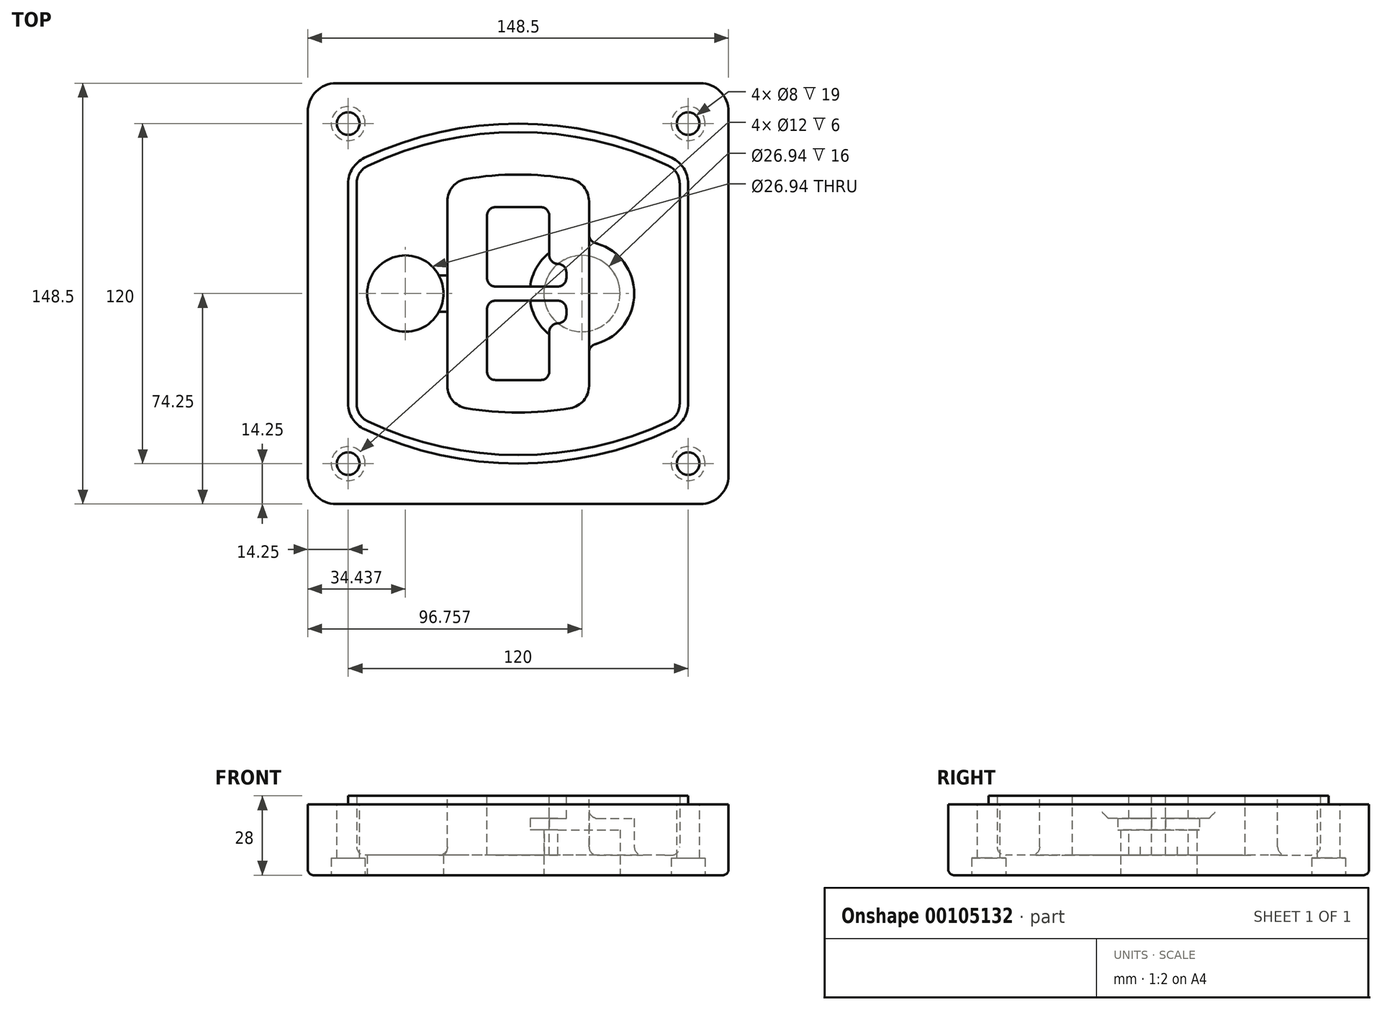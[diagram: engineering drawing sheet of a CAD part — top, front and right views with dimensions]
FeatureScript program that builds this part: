
annotation { "Feature Type Name" : "Feature", "Feature Type Description" : "" }
export const myFeature = defineFeature(function(context is Context, id is Id, definition is map)
    precondition{}
    {
        {
            var Q0;
            Q0=qCreatedBy(makeId("Top.planeOp"),FACE);
            var sketch = newSketch(context, id + "F0", { "sketchPlane" : qUnion([Q0])});
            skPoint(sketch, "E0.rect.middle", {"position": v(0, 0) * mm});
            skLineSegment(sketch, "E1.bottom", {"start": v(-64.25, -74.25) * mm, "end": v(64.25, -74.25) * mm});
            skLineSegment(sketch, "E1.top", {"start": v(-64.25, 74.25) * mm, "end": v(64.25, 74.25) * mm});
            skLineSegment(sketch, "E1.left", {"start": v(-74.25, -64.25) * mm, "end": v(-74.25, 64.25) * mm});
            skLineSegment(sketch, "E1.right", {"start": v(74.25, -64.25) * mm, "end": v(74.25, 64.25) * mm});
            skLineSegment(sketch, "E2", {"start": v(-74.25, 74.25) * mm, "end": v(74.25, -74.25) * mm, "construction": true});
            skLineSegment(sketch, "E3", {"start": v(74.25, 74.25) * mm, "end": v(-74.25, -74.25) * mm, "construction": true});
            skCircle(sketch, "E4", {"center": v(-60, 60) * mm, "radius": 4 * mm});
            skCircle(sketch, "E5", {"center": v(60, 60) * mm, "radius": 4 * mm});
            skCircle(sketch, "E6", {"center": v(60, -60) * mm, "radius": 4 * mm});
            skCircle(sketch, "E7", {"center": v(-60, -60) * mm, "radius": 4 * mm});
            skLineSegment(sketch, "E8", {"start": v(-60, 60) * mm, "end": v(60, 60) * mm, "construction": true});
            skLineSegment(sketch, "E9", {"start": v(60, 60) * mm, "end": v(60, -60) * mm, "construction": true});
            skLineSegment(sketch, "E10", {"start": v(60, -60) * mm, "end": v(-60, -60) * mm, "construction": true});
            skLineSegment(sketch, "E11", {"start": v(-60, -60) * mm, "end": v(-60, 60) * mm, "construction": true});
            skLineSegment(sketch, "E12", {"start": v(-60, 38.83) * mm, "end": v(-60, -38.83) * mm});
            skLineSegment(sketch, "E13", {"start": v(60, 38.83) * mm, "end": v(60, -38.83) * mm});
            skArc(sketch, "E14", {"start": v(54.26, 47.88) * mm, "mid": v(0, 60) * mm, "end": v(-54.26, 47.88) * mm});
            skArc(sketch, "E15", {"start": v(-54.26, -47.88) * mm, "mid": v(0, -60) * mm, "end": v(54.26, -47.88) * mm});
            skLineSegment(sketch, "E16", {"start": v(-60, 0) * mm, "end": v(60, 0) * mm, "construction": true});
            skPoint(sketch, "E17.visualSharp", {"position": v(-60, -45) * mm});
            skArc(sketch, "E17.filletArc", {"start": v(-60, -38.83) * mm, "mid": v(-58.44, -44.2) * mm, "end": v(-54.26, -47.88) * mm});
            skPoint(sketch, "E18.visualSharp", {"position": v(-60, 45) * mm});
            skArc(sketch, "E18.filletArc", {"start": v(-54.26, 47.88) * mm, "mid": v(-58.44, 44.2) * mm, "end": v(-60, 38.83) * mm});
            skPoint(sketch, "E19.visualSharp", {"position": v(60, 45) * mm});
            skArc(sketch, "E19.filletArc", {"start": v(60, 38.83) * mm, "mid": v(58.44, 44.2) * mm, "end": v(54.26, 47.88) * mm});
            skPoint(sketch, "E20.visualSharp", {"position": v(60, -45) * mm});
            skArc(sketch, "E20.filletArc", {"start": v(54.26, -47.88) * mm, "mid": v(58.44, -44.2) * mm, "end": v(60, -38.83) * mm});
            skPoint(sketch, "E21.visualSharp", {"position": v(-74.25, 74.25) * mm});
            skArc(sketch, "E21.filletArc", {"start": v(-64.25, 74.25) * mm, "mid": v(-71.32, 71.32) * mm, "end": v(-74.25, 64.25) * mm});
            skPoint(sketch, "E22.visualSharp", {"position": v(74.25, 74.25) * mm});
            skArc(sketch, "E22.filletArc", {"start": v(74.25, 64.25) * mm, "mid": v(71.32, 71.32) * mm, "end": v(64.25, 74.25) * mm});
            skPoint(sketch, "E23.visualSharp", {"position": v(74.25, -74.25) * mm});
            skArc(sketch, "E23.filletArc", {"start": v(64.25, -74.25) * mm, "mid": v(71.32, -71.32) * mm, "end": v(74.25, -64.25) * mm});
            skPoint(sketch, "E24.visualSharp", {"position": v(-74.25, -74.25) * mm});
            skArc(sketch, "E24.filletArc", {"start": v(-74.25, -64.25) * mm, "mid": v(-71.32, -71.32) * mm, "end": v(-64.25, -74.25) * mm});
            skArc(sketch, "E25.0", {"start": v(57, 38.83) * mm, "mid": v(55.9, 42.58) * mm, "end": v(52.98, 45.17) * mm});
            skLineSegment(sketch, "E25.1", {"start": v(57, 38.83) * mm, "end": v(57, -38.83) * mm});
            skArc(sketch, "E25.2", {"start": v(52.98, -45.17) * mm, "mid": v(55.9, -42.58) * mm, "end": v(57, -38.83) * mm});
            skArc(sketch, "E25.3", {"start": v(-52.98, -45.17) * mm, "mid": v(0, -57) * mm, "end": v(52.98, -45.17) * mm});
            skArc(sketch, "E25.4", {"start": v(-57, -38.83) * mm, "mid": v(-55.9, -42.58) * mm, "end": v(-52.98, -45.17) * mm});
            skArc(sketch, "E25.5", {"start": v(52.98, 45.17) * mm, "mid": v(0, 57) * mm, "end": v(-52.98, 45.17) * mm});
            skLineSegment(sketch, "E25.6", {"start": v(-57, 38.83) * mm, "end": v(-57, -38.83) * mm});
            skArc(sketch, "E25.7", {"start": v(-52.98, 45.17) * mm, "mid": v(-55.9, 42.58) * mm, "end": v(-57, 38.83) * mm});
            skArc(sketch, "E26.0", {"start": v(-55.96, 51.5) * mm, "mid": v(-61.82, 46.33) * mm, "end": v(-64, 38.83) * mm});
            skArc(sketch, "E26.1", {"start": v(55.96, 51.5) * mm, "mid": v(0, 64) * mm, "end": v(-55.96, 51.5) * mm});
            skArc(sketch, "E26.2", {"start": v(64, 38.83) * mm, "mid": v(61.82, 46.33) * mm, "end": v(55.96, 51.5) * mm});
            skLineSegment(sketch, "E26.3", {"start": v(64, 38.83) * mm, "end": v(64, -38.83) * mm});
            skArc(sketch, "E26.4", {"start": v(55.96, -51.5) * mm, "mid": v(61.82, -46.33) * mm, "end": v(64, -38.83) * mm});
            skLineSegment(sketch, "E26.5", {"start": v(-64, 38.83) * mm, "end": v(-64, -38.83) * mm});
            skArc(sketch, "E26.6", {"start": v(-55.96, -51.5) * mm, "mid": v(0, -64) * mm, "end": v(55.96, -51.5) * mm});
            skArc(sketch, "E26.7", {"start": v(-64, -38.83) * mm, "mid": v(-61.82, -46.33) * mm, "end": v(-55.96, -51.5) * mm});
            skSolve(sketch);
        }
        {
            var Q0;
            Q0=makeQuery(id+"F0.imprint","IMPRINT",FACE,{"disambiguationData":[TD([[makeQuery(id+"F0.imprint","IMPRINT",EDGE,{"derivedFrom":sQuery(id+"F0.wireOp",EDGE,"E1.bottom")}),1.0]])]});
            var Q1;
            Q1=makeQuery(id+"F0.imprint","IMPRINT",FACE,{"disambiguationData":[TD([[makeQuery(id+"F0.imprint","IMPRINT",EDGE,{"derivedFrom":sQuery(id+"F0.wireOp",EDGE,"E12")}),1.0]])]});
            var Q2;
            Q2=makeQuery(id+"F0.imprint","IMPRINT",FACE,{"disambiguationData":[TD([[makeQuery(id+"F0.imprint","IMPRINT",EDGE,{"derivedFrom":sQuery(id+"F0.wireOp",EDGE,"E25.0")}),1.0]])]});
            var Q3;
            Q3=makeQuery(id+"F0.imprint","IMPRINT",FACE,{"disambiguationData":[TD([[makeQuery(id+"F0.imprint","IMPRINT",EDGE,{"derivedFrom":sQuery(id+"F0.wireOp",EDGE,"E12")}),-1.0]])]});
            extrude(context, id + "F1", {"entities" : qUnion([Q0, Q1, Q2, Q3]), "oppositeDirection" : true, "depth" : 25 * mm});
        }
        {
            var Q0;
            Q0=makeQuery(id+"F0.imprint","IMPRINT",FACE,{"disambiguationData":[TD([[makeQuery(id+"F0.imprint","IMPRINT",EDGE,{"derivedFrom":sQuery(id+"F0.wireOp",EDGE,"E12")}),1.0]])]});
            extrude(context, id + "F2", {"entities" : qUnion([Q0]), "operationType" : NewBodyOperationType.ADD, "depth" : 3 * mm});
        }
        {
            var Q0;
            Q0=makeQuery(id+"F0.imprint","IMPRINT",FACE,{"disambiguationData":[TD([[makeQuery(id+"F0.imprint","IMPRINT",EDGE,{"derivedFrom":sQuery(id+"F0.wireOp",EDGE,"E25.0")}),1.0]])]});
            extrude(context, id + "F3", {"entities" : qUnion([Q0]), "operationType" : NewBodyOperationType.REMOVE, "oppositeDirection" : true, "depth" : 18 * mm});
        }
        {
            var Q0;
            Q0=makeQuery(id+"F2.opExtrude","CAP_FACE",FACE,{"disambiguationData":[OSD([sQuery(id+"F0.wireOp",EDGE,"E12"),sQuery(id+"F0.wireOp",EDGE,"E13"),sQuery(id+"F0.wireOp",EDGE,"E14"),sQuery(id+"F0.wireOp",EDGE,"E15"),sQuery(id+"F0.wireOp",EDGE,"E17.filletArc"),sQuery(id+"F0.wireOp",EDGE,"E18.filletArc"),sQuery(id+"F0.wireOp",EDGE,"E19.filletArc"),sQuery(id+"F0.wireOp",EDGE,"E20.filletArc"),sQuery(id+"F0.wireOp",EDGE,"E25.0"),sQuery(id+"F0.wireOp",EDGE,"E25.1"),sQuery(id+"F0.wireOp",EDGE,"E25.2"),sQuery(id+"F0.wireOp",EDGE,"E25.3"),sQuery(id+"F0.wireOp",EDGE,"E25.4"),sQuery(id+"F0.wireOp",EDGE,"E25.5"),sQuery(id+"F0.wireOp",EDGE,"E25.6"),sQuery(id+"F0.wireOp",EDGE,"E25.7")])],"isStart":false});
            var sketch = newSketch(context, id + "F4", { "sketchPlane" : qUnion([Q0])});
            skArc(sketch, "E27.0", {"start": v(-18.34, -40.45) * mm, "mid": v(0, -42) * mm, "end": v(18.34, -40.45) * mm});
            skArc(sketch, "E28.0", {"start": v(18.34, 40.45) * mm, "mid": v(0, 42) * mm, "end": v(-18.34, 40.45) * mm});
            skLineSegment(sketch, "E29", {"start": v(-25, 32.57) * mm, "end": v(-25, -32.57) * mm});
            skLineSegment(sketch, "E30", {"start": v(25, 32.57) * mm, "end": v(25, -32.57) * mm});
            skLineSegment(sketch, "E31", {"start": v(-25, 39.1) * mm, "end": v(25, 39.1) * mm, "construction": true});
            skLineSegment(sketch, "E32", {"start": v(-25, -39.1) * mm, "end": v(25, -39.1) * mm, "construction": true});
            skPoint(sketch, "E33.visualSharp", {"position": v(-25, 39.1) * mm});
            skArc(sketch, "E33.filletArc", {"start": v(-18.34, 40.45) * mm, "mid": v(-23.11, 37.73) * mm, "end": v(-25, 32.57) * mm});
            skPoint(sketch, "E34.visualSharp", {"position": v(25, 39.1) * mm});
            skArc(sketch, "E34.filletArc", {"start": v(25, 32.57) * mm, "mid": v(23.11, 37.73) * mm, "end": v(18.34, 40.45) * mm});
            skPoint(sketch, "E35.visualSharp", {"position": v(25, -39.1) * mm});
            skArc(sketch, "E35.filletArc", {"start": v(18.34, -40.45) * mm, "mid": v(23.11, -37.73) * mm, "end": v(25, -32.57) * mm});
            skPoint(sketch, "E36.visualSharp", {"position": v(-25, -39.1) * mm});
            skArc(sketch, "E36.filletArc", {"start": v(-25, -32.57) * mm, "mid": v(-23.11, -37.73) * mm, "end": v(-18.34, -40.45) * mm});
            skArc(sketch, "E37.0", {"start": v(52.98, 45.17) * mm, "mid": v(0, 57) * mm, "end": v(-52.98, 45.17) * mm});
            skArc(sketch, "E37.1", {"start": v(-52.98, 45.17) * mm, "mid": v(-55.9, 42.58) * mm, "end": v(-57, 38.83) * mm});
            skLineSegment(sketch, "E37.2", {"start": v(-57, 38.83) * mm, "end": v(-57, -38.83) * mm});
            skArc(sketch, "E37.3", {"start": v(-57, -38.83) * mm, "mid": v(-55.9, -42.58) * mm, "end": v(-52.98, -45.17) * mm});
            skArc(sketch, "E37.4", {"start": v(-52.98, -45.17) * mm, "mid": v(0, -57) * mm, "end": v(52.98, -45.17) * mm});
            skArc(sketch, "E37.5", {"start": v(52.98, -45.17) * mm, "mid": v(55.9, -42.58) * mm, "end": v(57, -38.83) * mm});
            skLineSegment(sketch, "E37.6", {"start": v(57, 38.83) * mm, "end": v(57, -38.83) * mm});
            skArc(sketch, "E37.7", {"start": v(57, 38.83) * mm, "mid": v(55.9, 42.58) * mm, "end": v(52.98, 45.17) * mm});
            skLineSegment(sketch, "E38.0", {"start": v(23, 32.57) * mm, "end": v(23, -32.57) * mm});
            skArc(sketch, "E38.1", {"start": v(18, -38.48) * mm, "mid": v(21.58, -36.44) * mm, "end": v(23, -32.57) * mm});
            skArc(sketch, "E38.2", {"start": v(-18, -38.48) * mm, "mid": v(0, -40) * mm, "end": v(18, -38.48) * mm});
            skArc(sketch, "E38.3", {"start": v(-23, -32.57) * mm, "mid": v(-21.58, -36.44) * mm, "end": v(-18, -38.48) * mm});
            skLineSegment(sketch, "E38.4", {"start": v(-23, 32.57) * mm, "end": v(-23, -32.57) * mm});
            skArc(sketch, "E38.5", {"start": v(23, 32.57) * mm, "mid": v(21.58, 36.44) * mm, "end": v(18, 38.48) * mm});
            skArc(sketch, "E38.6", {"start": v(-18, 38.48) * mm, "mid": v(-21.58, 36.44) * mm, "end": v(-23, 32.57) * mm});
            skArc(sketch, "E38.7", {"start": v(18, 38.48) * mm, "mid": v(0, 40) * mm, "end": v(-18, 38.48) * mm});
            skArc(sketch, "E39.0", {"start": v(21, 32.57) * mm, "mid": v(20.06, 35.15) * mm, "end": v(17.67, 36.5) * mm});
            skLineSegment(sketch, "E39.1", {"start": v(21, 32.57) * mm, "end": v(21, -32.57) * mm});
            skArc(sketch, "E39.2", {"start": v(17.67, -36.5) * mm, "mid": v(20.06, -35.15) * mm, "end": v(21, -32.57) * mm});
            skArc(sketch, "E39.3", {"start": v(-17.67, -36.5) * mm, "mid": v(0, -38) * mm, "end": v(17.67, -36.5) * mm});
            skArc(sketch, "E39.4", {"start": v(-21, -32.57) * mm, "mid": v(-20.06, -35.15) * mm, "end": v(-17.67, -36.5) * mm});
            skArc(sketch, "E39.5", {"start": v(17.67, 36.5) * mm, "mid": v(0, 38) * mm, "end": v(-17.67, 36.5) * mm});
            skLineSegment(sketch, "E39.6", {"start": v(-21, 32.57) * mm, "end": v(-21, -32.57) * mm});
            skArc(sketch, "E39.7", {"start": v(-17.67, 36.5) * mm, "mid": v(-20.06, 35.15) * mm, "end": v(-21, 32.57) * mm});
            skLineSegment(sketch, "E40", {"start": v(-25, 0) * mm, "end": v(25, 0) * mm, "construction": true});
            skLineSegment(sketch, "E41", {"start": v(-11, 5.5) * mm, "end": v(-11, 27.5) * mm});
            skLineSegment(sketch, "E42", {"start": v(-8, 30.5) * mm, "end": v(8, 30.5) * mm});
            skLineSegment(sketch, "E43", {"start": v(11, 27.5) * mm, "end": v(11, 13.5) * mm});
            skLineSegment(sketch, "E44", {"start": v(14, 10.5) * mm, "end": v(14, 10.5) * mm});
            skLineSegment(sketch, "E45", {"start": v(17, 7.5) * mm, "end": v(17, 5.5) * mm});
            skLineSegment(sketch, "E46", {"start": v(14, 2.5) * mm, "end": v(-8, 2.5) * mm});
            skPoint(sketch, "E47.visualSharp", {"position": v(-11, 30.5) * mm});
            skArc(sketch, "E47.filletArc", {"start": v(-8, 30.5) * mm, "mid": v(-10.12, 29.62) * mm, "end": v(-11, 27.5) * mm});
            skPoint(sketch, "E48.visualSharp", {"position": v(11, 30.5) * mm});
            skArc(sketch, "E48.filletArc", {"start": v(11, 27.5) * mm, "mid": v(10.12, 29.62) * mm, "end": v(8, 30.5) * mm});
            skPoint(sketch, "E49.visualSharp", {"position": v(11, 10.5) * mm});
            skArc(sketch, "E49.filletArc", {"start": v(11, 13.5) * mm, "mid": v(11.88, 11.38) * mm, "end": v(14, 10.5) * mm});
            skPoint(sketch, "E50.visualSharp", {"position": v(17, 10.5) * mm});
            skArc(sketch, "E50.filletArc", {"start": v(17, 7.5) * mm, "mid": v(16.12, 9.62) * mm, "end": v(14, 10.5) * mm});
            skPoint(sketch, "E51.visualSharp", {"position": v(17, 2.5) * mm});
            skArc(sketch, "E51.filletArc", {"start": v(14, 2.5) * mm, "mid": v(16.12, 3.38) * mm, "end": v(17, 5.5) * mm});
            skPoint(sketch, "E52.visualSharp", {"position": v(-11, 2.5) * mm});
            skArc(sketch, "E52.filletArc", {"start": v(-11, 5.5) * mm, "mid": v(-10.12, 3.38) * mm, "end": v(-8, 2.5) * mm});
            skLineSegment(sketch, "E53.0.MirrorCS", {"start": v(14, -2.5) * mm, "end": v(-8, -2.5) * mm});
            skArc(sketch, "E54.0.MirrorCS", {"start": v(-11, -5.5) * mm, "mid": v(-10.12, -3.38) * mm, "end": v(-8, -2.5) * mm});
            skLineSegment(sketch, "E55.0.MirrorCS", {"start": v(-11, -5.5) * mm, "end": v(-11, -27.5) * mm});
            skArc(sketch, "E56.0.MirrorCS", {"start": v(-8, -30.5) * mm, "mid": v(-10.12, -29.62) * mm, "end": v(-11, -27.5) * mm});
            skLineSegment(sketch, "E57.0.MirrorCS", {"start": v(-8, -30.5) * mm, "end": v(8, -30.5) * mm});
            skArc(sketch, "E58.0.MirrorCS", {"start": v(11, -27.5) * mm, "mid": v(10.12, -29.62) * mm, "end": v(8, -30.5) * mm});
            skLineSegment(sketch, "E59.0.MirrorCS", {"start": v(11, -27.5) * mm, "end": v(11, -13.5) * mm});
            skArc(sketch, "E60.0.MirrorCS", {"start": v(11, -13.5) * mm, "mid": v(11.88, -11.38) * mm, "end": v(14, -10.5) * mm});
            skArc(sketch, "E61.0.MirrorCS", {"start": v(17, -7.5) * mm, "mid": v(16.12, -9.62) * mm, "end": v(14, -10.5) * mm});
            skLineSegment(sketch, "E62.0.MirrorCS", {"start": v(17, -7.5) * mm, "end": v(17, -5.5) * mm});
            skArc(sketch, "E63.0.MirrorCS", {"start": v(14, -2.5) * mm, "mid": v(16.12, -3.38) * mm, "end": v(17, -5.5) * mm});
            skSolve(sketch);
        }
        {
            var Q0;
            Q0=makeQuery(id+"F4.imprint","IMPRINT",FACE,{"disambiguationData":[TD([[makeQuery(id+"F4.imprint","IMPRINT",EDGE,{"derivedFrom":sQuery(id+"F4.wireOp",EDGE,"E27.0")}),1.0]])]});
            var Q1;
            Q1=makeQuery(id+"F4.imprint","IMPRINT",FACE,{"disambiguationData":[TD([[makeQuery(id+"F4.imprint","IMPRINT",EDGE,{"derivedFrom":sQuery(id+"F4.wireOp",EDGE,"E38.0")}),-1.0]])]});
            var Q2;
            Q2=makeQuery(id+"F4.imprint","IMPRINT",FACE,{"disambiguationData":[TD([[makeQuery(id+"F4.imprint","IMPRINT",EDGE,{"derivedFrom":sQuery(id+"F4.wireOp",EDGE,"E39.0")}),1.0]])]});
            extrude(context, id + "F5", {"entities" : qUnion([Q0, Q1, Q2]), "operationType" : NewBodyOperationType.ADD, "endBound" : BoundingType.UP_TO_NEXT, "oppositeDirection" : true, "depth" : 25 * mm});
        }
        {
            var Q0;
            Q0=makeQuery(id+"F1.opExtrude","CAP_FACE",FACE,{"disambiguationData":[OSD([sQuery(id+"F0.wireOp",EDGE,"E1.bottom"),sQuery(id+"F0.wireOp",EDGE,"E1.top"),sQuery(id+"F0.wireOp",EDGE,"E1.left"),sQuery(id+"F0.wireOp",EDGE,"E1.right"),sQuery(id+"F0.wireOp",EDGE,"E4"),sQuery(id+"F0.wireOp",EDGE,"E5"),sQuery(id+"F0.wireOp",EDGE,"E6"),sQuery(id+"F0.wireOp",EDGE,"E7"),sQuery(id+"F0.wireOp",EDGE,"E21.filletArc"),sQuery(id+"F0.wireOp",EDGE,"E22.filletArc"),sQuery(id+"F0.wireOp",EDGE,"E23.filletArc"),sQuery(id+"F0.wireOp",EDGE,"E24.filletArc")])],"isStart":false});
            var sketch = newSketch(context, id + "F6", { "sketchPlane" : qUnion([Q0])});
            skCircle(sketch, "E64", {"center": v(22.5, 0) * mm, "radius": 13.47 * mm});
            skCircle(sketch, "E65", {"center": v(-39.81, 0) * mm, "radius": 13.47 * mm});
            skLineSegment(sketch, "E66", {"start": v(74.25, 0) * mm, "end": v(-74.25, 0) * mm});
            skCircle(sketch, "E67", {"center": v(22.5, 0) * mm, "radius": 18.47 * mm});
            skCircle(sketch, "E68", {"center": v(60, -60) * mm, "radius": 6 * mm});
            skCircle(sketch, "E69", {"center": v(-60, -60) * mm, "radius": 6 * mm});
            skCircle(sketch, "E70", {"center": v(-60, 60) * mm, "radius": 6 * mm});
            skCircle(sketch, "E71", {"center": v(60, 60) * mm, "radius": 6 * mm});
            skSolve(sketch);
        }
        {
            var Q0;
            {var subQ1=sQuery(id+"F6.wireOp",EDGE,"E66");var subQ4=sQuery(id+"F6.wireOp",EDGE,"E64");var subQ6=makeQuery(id+"F6.imprint","INTERSECT",VERTEX,{"disambiguationData":[OD(0.0)],"derivedFrom":[subQ4,subQ1]});Q0=makeQuery(id+"F6.imprint","IMPRINT",FACE,{"disambiguationData":[TD([[makeQuery(id+"F6.imprint","IMPRINT",EDGE,{"disambiguationData":[TD([[subQ6,-1.0]])],"derivedFrom":subQ4}),-1.0]])]});}
            var Q1;
            {var subQ0=sQuery(id+"F6.wireOp",EDGE,"E66");var subQ1=sQuery(id+"F6.wireOp",EDGE,"E64");var subQ3=makeQuery(id+"F6.imprint","INTERSECT",VERTEX,{"disambiguationData":[OD(0.0)],"derivedFrom":[subQ1,subQ0]});Q1=makeQuery(id+"F6.imprint","IMPRINT",FACE,{"disambiguationData":[TD([[makeQuery(id+"F6.imprint","IMPRINT",EDGE,{"disambiguationData":[TD([[subQ3,-1.0]])],"derivedFrom":subQ1}),1.0]])]});}
            var Q2;
            {var subQ0=sQuery(id+"F6.wireOp",EDGE,"E66");var subQ1=sQuery(id+"F6.wireOp",EDGE,"E64");var subQ3=makeQuery(id+"F6.imprint","INTERSECT",VERTEX,{"disambiguationData":[OD(0.0)],"derivedFrom":[subQ1,subQ0]});Q2=makeQuery(id+"F6.imprint","IMPRINT",FACE,{"disambiguationData":[TD([[makeQuery(id+"F6.imprint","IMPRINT",EDGE,{"disambiguationData":[TD([[subQ3,1.0]])],"derivedFrom":subQ1}),1.0]])]});}
            var Q3;
            {var subQ1=sQuery(id+"F6.wireOp",EDGE,"E66");var subQ4=sQuery(id+"F6.wireOp",EDGE,"E64");var subQ6=makeQuery(id+"F6.imprint","INTERSECT",VERTEX,{"disambiguationData":[OD(0.0)],"derivedFrom":[subQ4,subQ1]});Q3=makeQuery(id+"F6.imprint","IMPRINT",FACE,{"disambiguationData":[TD([[makeQuery(id+"F6.imprint","IMPRINT",EDGE,{"disambiguationData":[TD([[subQ6,1.0]])],"derivedFrom":subQ4}),-1.0]])]});}
            extrude(context, id + "F7", {"entities" : qUnion([Q0, Q1, Q2, Q3]), "operationType" : NewBodyOperationType.ADD, "oppositeDirection" : true, "depth" : 20 * mm});
        }
        {
            var Q0;
            {var subQ0=sQuery(id+"F6.wireOp",EDGE,"E66");var subQ1=sQuery(id+"F6.wireOp",EDGE,"E64");var subQ3=makeQuery(id+"F6.imprint","INTERSECT",VERTEX,{"disambiguationData":[OD(0.0)],"derivedFrom":[subQ1,subQ0]});Q0=makeQuery(id+"F6.imprint","IMPRINT",FACE,{"disambiguationData":[TD([[makeQuery(id+"F6.imprint","IMPRINT",EDGE,{"disambiguationData":[TD([[subQ3,-1.0]])],"derivedFrom":subQ1}),1.0]])]});}
            var Q1;
            {var subQ0=sQuery(id+"F6.wireOp",EDGE,"E66");var subQ1=sQuery(id+"F6.wireOp",EDGE,"E64");var subQ3=makeQuery(id+"F6.imprint","INTERSECT",VERTEX,{"disambiguationData":[OD(0.0)],"derivedFrom":[subQ1,subQ0]});Q1=makeQuery(id+"F6.imprint","IMPRINT",FACE,{"disambiguationData":[TD([[makeQuery(id+"F6.imprint","IMPRINT",EDGE,{"disambiguationData":[TD([[subQ3,1.0]])],"derivedFrom":subQ1}),1.0]])]});}
            extrude(context, id + "F8", {"entities" : qUnion([Q0, Q1]), "operationType" : NewBodyOperationType.REMOVE, "oppositeDirection" : true, "depth" : 16 * mm});
        }
        {
            var Q0;
            {var subQ0=sQuery(id+"F6.wireOp",EDGE,"E66");var subQ1=sQuery(id+"F6.wireOp",EDGE,"E65");var subQ3=makeQuery(id+"F6.imprint","INTERSECT",VERTEX,{"disambiguationData":[OD(0.0)],"derivedFrom":[subQ1,subQ0]});Q0=makeQuery(id+"F6.imprint","IMPRINT",FACE,{"disambiguationData":[TD([[makeQuery(id+"F6.imprint","IMPRINT",EDGE,{"disambiguationData":[TD([[subQ3,-1.0]])],"derivedFrom":subQ1}),1.0]])]});}
            var Q1;
            {var subQ0=sQuery(id+"F6.wireOp",EDGE,"E66");var subQ1=sQuery(id+"F6.wireOp",EDGE,"E65");var subQ3=makeQuery(id+"F6.imprint","INTERSECT",VERTEX,{"disambiguationData":[OD(0.0)],"derivedFrom":[subQ1,subQ0]});Q1=makeQuery(id+"F6.imprint","IMPRINT",FACE,{"disambiguationData":[TD([[makeQuery(id+"F6.imprint","IMPRINT",EDGE,{"disambiguationData":[TD([[subQ3,1.0]])],"derivedFrom":subQ1}),1.0]])]});}
            extrude(context, id + "F9", {"entities" : qUnion([Q0, Q1]), "operationType" : NewBodyOperationType.REMOVE, "oppositeDirection" : true, "depth" : 25 * mm});
        }
        {
            var Q0;
            Q0=makeQuery(id+"F6.imprint","IMPRINT",FACE,{"disambiguationData":[TD([[makeQuery(id+"F6.imprint","IMPRINT",EDGE,{"derivedFrom":sQuery(id+"F6.wireOp",EDGE,"E68")}),1.0]])]});
            var Q1;
            Q1=makeQuery(id+"F6.imprint","IMPRINT",FACE,{"disambiguationData":[TD([[makeQuery(id+"F6.imprint","IMPRINT",EDGE,{"derivedFrom":makeQuery(id+"F1.opExtrude","CAP_EDGE",EDGE,{"disambiguationData":[OSD([sQuery(id+"F0.wireOp",EDGE,"E5")])],"isStart":false})}),-1.0]])]});
            var Q2;
            Q2=makeQuery(id+"F6.imprint","IMPRINT",FACE,{"disambiguationData":[TD([[makeQuery(id+"F6.imprint","IMPRINT",EDGE,{"derivedFrom":sQuery(id+"F6.wireOp",EDGE,"E69")}),1.0]])]});
            var Q3;
            Q3=makeQuery(id+"F6.imprint","IMPRINT",FACE,{"disambiguationData":[TD([[makeQuery(id+"F6.imprint","IMPRINT",EDGE,{"derivedFrom":makeQuery(id+"F1.opExtrude","CAP_EDGE",EDGE,{"disambiguationData":[OSD([sQuery(id+"F0.wireOp",EDGE,"E4")])],"isStart":false})}),-1.0]])]});
            var Q4;
            Q4=makeQuery(id+"F6.imprint","IMPRINT",FACE,{"disambiguationData":[TD([[makeQuery(id+"F6.imprint","IMPRINT",EDGE,{"derivedFrom":sQuery(id+"F6.wireOp",EDGE,"E70")}),1.0]])]});
            var Q5;
            Q5=makeQuery(id+"F6.imprint","IMPRINT",FACE,{"disambiguationData":[TD([[makeQuery(id+"F6.imprint","IMPRINT",EDGE,{"derivedFrom":makeQuery(id+"F1.opExtrude","CAP_EDGE",EDGE,{"disambiguationData":[OSD([sQuery(id+"F0.wireOp",EDGE,"E7")])],"isStart":false})}),-1.0]])]});
            var Q6;
            Q6=makeQuery(id+"F6.imprint","IMPRINT",FACE,{"disambiguationData":[TD([[makeQuery(id+"F6.imprint","IMPRINT",EDGE,{"derivedFrom":sQuery(id+"F6.wireOp",EDGE,"E71")}),1.0]])]});
            var Q7;
            Q7=makeQuery(id+"F6.imprint","IMPRINT",FACE,{"disambiguationData":[TD([[makeQuery(id+"F6.imprint","IMPRINT",EDGE,{"derivedFrom":makeQuery(id+"F1.opExtrude","CAP_EDGE",EDGE,{"disambiguationData":[OSD([sQuery(id+"F0.wireOp",EDGE,"E6")])],"isStart":false})}),-1.0]])]});
            extrude(context, id + "F10", {"entities" : qUnion([Q0, Q1, Q2, Q3, Q4, Q5, Q6, Q7]), "operationType" : NewBodyOperationType.REMOVE, "oppositeDirection" : true, "depth" : 6 * mm});
        }
        {
            var Q0;
            Q0=makeQuery(id+"F8.boolean.opBoolean","COPY",FACE,{"derivedFrom":makeQuery(id+"F8.opExtrude","CAP_FACE",FACE,{"disambiguationData":[OSD([sQuery(id+"F6.wireOp",EDGE,"E64")])],"isStart":false})});
            var sketch = newSketch(context, id + "F11", { "sketchPlane" : qUnion([Q0])});
            skArc(sketch, "E72.0", {"start": v(11, 14.45) * mm, "mid": v(6.45, 9.13) * mm, "end": v(4.2, 2.5) * mm});
            skArc(sketch, "E72.1", {"start": v(4.2, -2.5) * mm, "mid": v(6.45, -9.13) * mm, "end": v(11, -14.45) * mm});
            skLineSegment(sketch, "E73", {"start": v(4.2, -2.5) * mm, "end": v(14, -2.5) * mm});
            skLineSegment(sketch, "E74.0", {"start": v(14, 2.5) * mm, "end": v(4.2, 2.5) * mm});
            skArc(sketch, "E74.1", {"start": v(14, 2.5) * mm, "mid": v(16.12, 3.38) * mm, "end": v(17, 5.5) * mm});
            skLineSegment(sketch, "E74.2", {"start": v(17, 7.5) * mm, "end": v(17, 5.5) * mm});
            skArc(sketch, "E74.3", {"start": v(17, 7.5) * mm, "mid": v(16.12, 9.62) * mm, "end": v(14, 10.5) * mm});
            skArc(sketch, "E74.4", {"start": v(11, 13.5) * mm, "mid": v(11.88, 11.38) * mm, "end": v(14, 10.5) * mm});
            skLineSegment(sketch, "E74.5", {"start": v(11, 14.45) * mm, "end": v(11, 13.5) * mm});
            skLineSegment(sketch, "E74.7", {"start": v(14, -2.5) * mm, "end": v(4.2, -2.5) * mm});
            skArc(sketch, "E74.8", {"start": v(14, -2.5) * mm, "mid": v(16.12, -3.38) * mm, "end": v(17, -5.5) * mm});
            skLineSegment(sketch, "E74.9", {"start": v(17, -7.5) * mm, "end": v(17, -5.5) * mm});
            skArc(sketch, "E74.10", {"start": v(17, -7.5) * mm, "mid": v(16.12, -9.62) * mm, "end": v(14, -10.5) * mm});
            skArc(sketch, "E74.11", {"start": v(11, -13.5) * mm, "mid": v(11.88, -11.38) * mm, "end": v(14, -10.5) * mm});
            skLineSegment(sketch, "E74.12", {"start": v(11, -14.45) * mm, "end": v(11, -13.5) * mm});
            skPoint(sketch, "E75.orphan", {"position": v(11, -27.5) * mm});
            skPoint(sketch, "E76.orphan", {"position": v(-8, -2.5) * mm});
            skPoint(sketch, "E77.orphan", {"position": v(-8, 2.5) * mm});
            skPoint(sketch, "E78.orphan", {"position": v(11, 27.5) * mm});
            skSolve(sketch);
        }
        {
            var Q0;
            {var subQ7=sQuery(id+"F11.wireOp",EDGE,"E72.0");var subQ14=sQuery(id+"F11.wireOp",EDGE,"E72.1");var subQ16=sQuery(id+"F11.wireOp",EDGE,"E74.1");var subQ18=sQuery(id+"F11.wireOp",EDGE,"E74.8");Q0=qUnion([makeQuery(id+"F11.imprint","IMPRINT",FACE,{"disambiguationData":[TD([[makeQuery(id+"F11.imprint","IMPRINT",EDGE,{"derivedFrom":subQ7}),1.0]])]}),makeQuery(id+"F11.imprint","IMPRINT",FACE,{"disambiguationData":[TD([[makeQuery(id+"F11.imprint","IMPRINT",EDGE,{"derivedFrom":subQ14}),1.0]])]}),makeQuery(id+"F11.imprint","IMPRINT",FACE,{"disambiguationData":[TD([[makeQuery(id+"F11.imprint","IMPRINT",EDGE,{"derivedFrom":subQ16}),1.0]])]}),makeQuery(id+"F11.imprint","IMPRINT",FACE,{"disambiguationData":[TD([[makeQuery(id+"F11.imprint","IMPRINT",EDGE,{"derivedFrom":subQ18}),-1.0]])]})]);}
            var Q1;
            Q1=makeQuery(id+"F5.boolean.opBoolean","SPLIT",FACE,{"disambiguationData":[TD([makeQuery(id+"F5.opExtrude","SWEPT_FACE",FACE,{"disambiguationData":[OSD([sQuery(id+"F4.wireOp",EDGE,"E41")])]})])],"derivedFrom":makeQuery(id+"F3.boolean.opBoolean","COPY",FACE,{"derivedFrom":makeQuery(id+"F3.opExtrude","CAP_FACE",FACE,{"disambiguationData":[OSD([sQuery(id+"F0.wireOp",EDGE,"E25.0"),sQuery(id+"F0.wireOp",EDGE,"E25.1"),sQuery(id+"F0.wireOp",EDGE,"E25.2"),sQuery(id+"F0.wireOp",EDGE,"E25.3"),sQuery(id+"F0.wireOp",EDGE,"E25.4"),sQuery(id+"F0.wireOp",EDGE,"E25.5"),sQuery(id+"F0.wireOp",EDGE,"E25.6"),sQuery(id+"F0.wireOp",EDGE,"E25.7")])],"isStart":false})})});
            extrude(context, id + "F12", {"entities" : qUnion([Q0]), "operationType" : NewBodyOperationType.REMOVE, "endBound" : BoundingType.UP_TO_SURFACE, "endBoundEntityFace" : qUnion([Q1]), "depth" : 25 * mm});
        }
        {
            var Q0;
            Q0=makeQuery(id+"F3.boolean.opBoolean","COPY",EDGE,{"derivedFrom":makeQuery(id+"F3.opExtrude","CAP_EDGE",EDGE,{"disambiguationData":[OSD([sQuery(id+"F0.wireOp",EDGE,"E25.6")])],"isStart":false})});
            var Q1;
            Q1=makeQuery(id+"F7.boolean.opBoolean","INTERSECT",EDGE,{"derivedFrom":[makeQuery(id+"F5.opExtrude","SWEPT_FACE",FACE,{"disambiguationData":[OSD([sQuery(id+"F4.wireOp",EDGE,"E30")])]}),makeQuery(id+"F7.opExtrude","CAP_FACE",FACE,{"disambiguationData":[OSD([sQuery(id+"F6.wireOp",EDGE,"E67")])],"isStart":false})]});
            var Q2;
            Q2=makeQuery(id+"F7.boolean.opBoolean","INTERSECT",EDGE,{"disambiguationData":[OD(1.0)],"derivedFrom":[makeQuery(id+"F5.opExtrude","SWEPT_FACE",FACE,{"disambiguationData":[OSD([sQuery(id+"F4.wireOp",EDGE,"E30")])]}),makeQuery(id+"F7.opExtrude","SWEPT_FACE",FACE,{"disambiguationData":[OSD([sQuery(id+"F6.wireOp",EDGE,"E67")])]})]});
            var Q3;
            {var subQ0=sQuery(id+"F4.wireOp",EDGE,"E30");Q3=makeQuery(id+"F7.boolean.opBoolean","SPLIT",EDGE,{"disambiguationData":[TD([makeQuery(id+"F5.opExtrude","SWEPT_FACE",FACE,{"disambiguationData":[OSD([sQuery(id+"F4.wireOp",EDGE,"E35.filletArc")])]})])],"derivedFrom":makeQuery(id+"F5.opExtrude","CAP_EDGE",EDGE,{"disambiguationData":[OSD([subQ0])],"isStart":false})});}
            var Q4;
            {var subQ0=sQuery(id+"F0.wireOp",EDGE,"E25.7");var subQ1=sQuery(id+"F0.wireOp",EDGE,"E25.1");var subQ2=sQuery(id+"F0.wireOp",EDGE,"E25.6");var subQ3=sQuery(id+"F0.wireOp",EDGE,"E25.5");var subQ4=sQuery(id+"F0.wireOp",EDGE,"E25.4");var subQ5=sQuery(id+"F0.wireOp",EDGE,"E25.0");var subQ6=sQuery(id+"F0.wireOp",EDGE,"E25.2");var subQ7=sQuery(id+"F0.wireOp",EDGE,"E25.3");Q4=makeQuery(id+"F7.boolean.opBoolean","INTERSECT",EDGE,{"derivedFrom":[makeQuery(id+"F5.boolean.opBoolean","SPLIT",FACE,{"disambiguationData":[TD([makeQuery(id+"F2.opExtrude","SWEPT_FACE",FACE,{"disambiguationData":[OSD([subQ5])]})])],"derivedFrom":makeQuery(id+"F3.boolean.opBoolean","COPY",FACE,{"derivedFrom":makeQuery(id+"F3.opExtrude","CAP_FACE",FACE,{"disambiguationData":[OSD([subQ5,subQ1,subQ6,subQ7,subQ4,subQ3,subQ2,subQ0])],"isStart":false})})}),makeQuery(id+"F7.opExtrude","SWEPT_FACE",FACE,{"disambiguationData":[OSD([sQuery(id+"F6.wireOp",EDGE,"E67")])]})]});}
            var Q5;
            Q5=makeQuery(id+"F7.boolean.opBoolean","INTERSECT",EDGE,{"disambiguationData":[OD(0.0)],"derivedFrom":[makeQuery(id+"F5.opExtrude","SWEPT_FACE",FACE,{"disambiguationData":[OSD([sQuery(id+"F4.wireOp",EDGE,"E30")])]}),makeQuery(id+"F7.opExtrude","SWEPT_FACE",FACE,{"disambiguationData":[OSD([sQuery(id+"F6.wireOp",EDGE,"E67")])]})]});
            fillet(context, id + "F13", {"entities" : qUnion([Q0, Q1, Q2, Q3, Q4, Q5]), "radius" : 3 * mm, "tangentPropagation" : true, "allowEdgeOverflow" : false});
        }
        {
            var Q0;
            Q0=makeQuery(id+"F1.opExtrude","CAP_EDGE",EDGE,{"disambiguationData":[OSD([sQuery(id+"F0.wireOp",EDGE,"E1.bottom")])],"isStart":false});
            fillet(context, id + "F14", {"entities" : qUnion([Q0]), "radius" : 2 * mm, "tangentPropagation" : true, "allowEdgeOverflow" : false});
        }
    });
